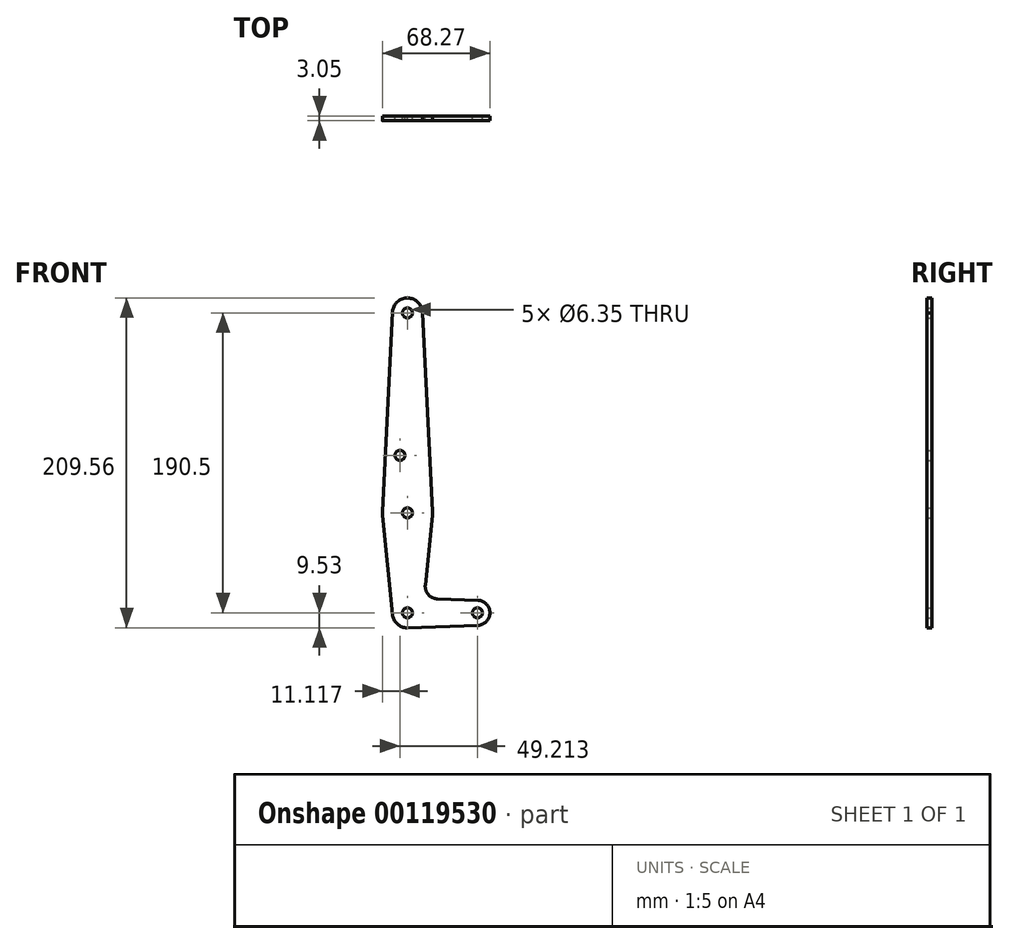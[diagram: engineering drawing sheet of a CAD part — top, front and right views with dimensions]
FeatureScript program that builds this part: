
annotation { "Feature Type Name" : "Feature", "Feature Type Description" : "" }
export const myFeature = defineFeature(function(context is Context, id is Id, definition is map)
    precondition{}
    {
        {
            var Q0;
            Q0=qCreatedBy(makeId("Front.planeOp"),FACE);
            var sketch = newSketch(context, id + "F0", { "sketchPlane" : qUnion([Q0])});
            skCircle(sketch, "E0", {"center": v(0, 190.5) * mm, "radius": 9.53 * mm});
            skCircle(sketch, "E1", {"center": v(0, 63.5) * mm, "radius": 15.88 * mm});
            skCircle(sketch, "E2", {"center": v(0, 0) * mm, "radius": 9.53 * mm});
            skCircle(sketch, "E3", {"center": v(44.45, 0) * mm, "radius": 7.94 * mm});
            skLineSegment(sketch, "E4", {"start": v(0, 190.5) * mm, "end": v(0, 63.5) * mm, "construction": true});
            skLineSegment(sketch, "E5", {"start": v(0, 0) * mm, "end": v(0, 63.5) * mm, "construction": true});
            skLineSegment(sketch, "E6", {"start": v(0, 0) * mm, "end": v(44.45, 0) * mm, "construction": true});
            skLineSegment(sketch, "E7", {"start": v(18.97, 8.85) * mm, "end": v(44.73, 7.93) * mm});
            skLineSegment(sketch, "E8", {"start": v(0, -9.53) * mm, "end": v(44.73, -7.93) * mm});
            skLineSegment(sketch, "E9", {"start": v(-9.51, 190.98) * mm, "end": v(-15.86, 64.3) * mm});
            skLineSegment(sketch, "E10", {"start": v(9.52, 190.5) * mm, "end": v(15.86, 64.3) * mm});
            skLineSegment(sketch, "E11", {"start": v(-15.8, 61.91) * mm, "end": v(-9.48, -0.95) * mm});
            skLineSegment(sketch, "E12", {"start": v(11.34, 17.59) * mm, "end": v(15.8, 61.91) * mm});
            skCircle(sketch, "E13", {"center": v(0, 190.5) * mm, "radius": 3.18 * mm});
            skCircle(sketch, "E14", {"center": v(0, 0) * mm, "radius": 3.18 * mm});
            skCircle(sketch, "E15", {"center": v(44.45, 0) * mm, "radius": 3.18 * mm});
            skCircle(sketch, "E16", {"center": v(0, 63.5) * mm, "radius": 3.18 * mm});
            skCircle(sketch, "E17", {"center": v(-4.76, 100.03) * mm, "radius": 3.18 * mm});
            skArc(sketch, "E18.filletArc", {"start": v(11.34, 17.59) * mm, "mid": v(13.26, 11.57) * mm, "end": v(18.97, 8.85) * mm});
            skSolve(sketch);
        }
        {
            var Q0;
            {var subQ1=sQuery(id+"F0.wireOp",EDGE,"E9");Q0=makeQuery(id+"F0.imprint","IMPRINT",FACE,{"disambiguationData":[TD([[makeQuery(id+"F0.imprint","IMPRINT",EDGE,{"derivedFrom":subQ1}),1.0]])]});}
            var Q1;
            Q1=makeQuery(id+"F0.imprint","IMPRINT",FACE,{"disambiguationData":[TD([[makeQuery(id+"F0.imprint","IMPRINT",EDGE,{"derivedFrom":sQuery(id+"F0.wireOp",EDGE,"E13")}),-1.0]])]});
            var Q2;
            Q2=makeQuery(id+"F0.imprint","IMPRINT",FACE,{"disambiguationData":[TD([[makeQuery(id+"F0.imprint","IMPRINT",EDGE,{"derivedFrom":sQuery(id+"F0.wireOp",EDGE,"E16")}),-1.0]])]});
            var Q3;
            {var subQ0=sQuery(id+"F0.wireOp",EDGE,"E7");Q3=makeQuery(id+"F0.imprint","IMPRINT",FACE,{"disambiguationData":[TD([[makeQuery(id+"F0.imprint","IMPRINT",EDGE,{"derivedFrom":subQ0}),-1.0]])]});}
            var Q4;
            Q4=makeQuery(id+"F0.imprint","IMPRINT",FACE,{"disambiguationData":[TD([[makeQuery(id+"F0.imprint","IMPRINT",EDGE,{"derivedFrom":sQuery(id+"F0.wireOp",EDGE,"E14")}),-1.0]])]});
            var Q5;
            Q5=makeQuery(id+"F0.imprint","IMPRINT",FACE,{"disambiguationData":[TD([[makeQuery(id+"F0.imprint","IMPRINT",EDGE,{"derivedFrom":sQuery(id+"F0.wireOp",EDGE,"E15")}),-1.0]])]});
            extrude(context, id + "F1", {"entities" : qUnion([Q0, Q1, Q2, Q3, Q4, Q5]), "depth" : 3.05 * mm});
        }
    });
